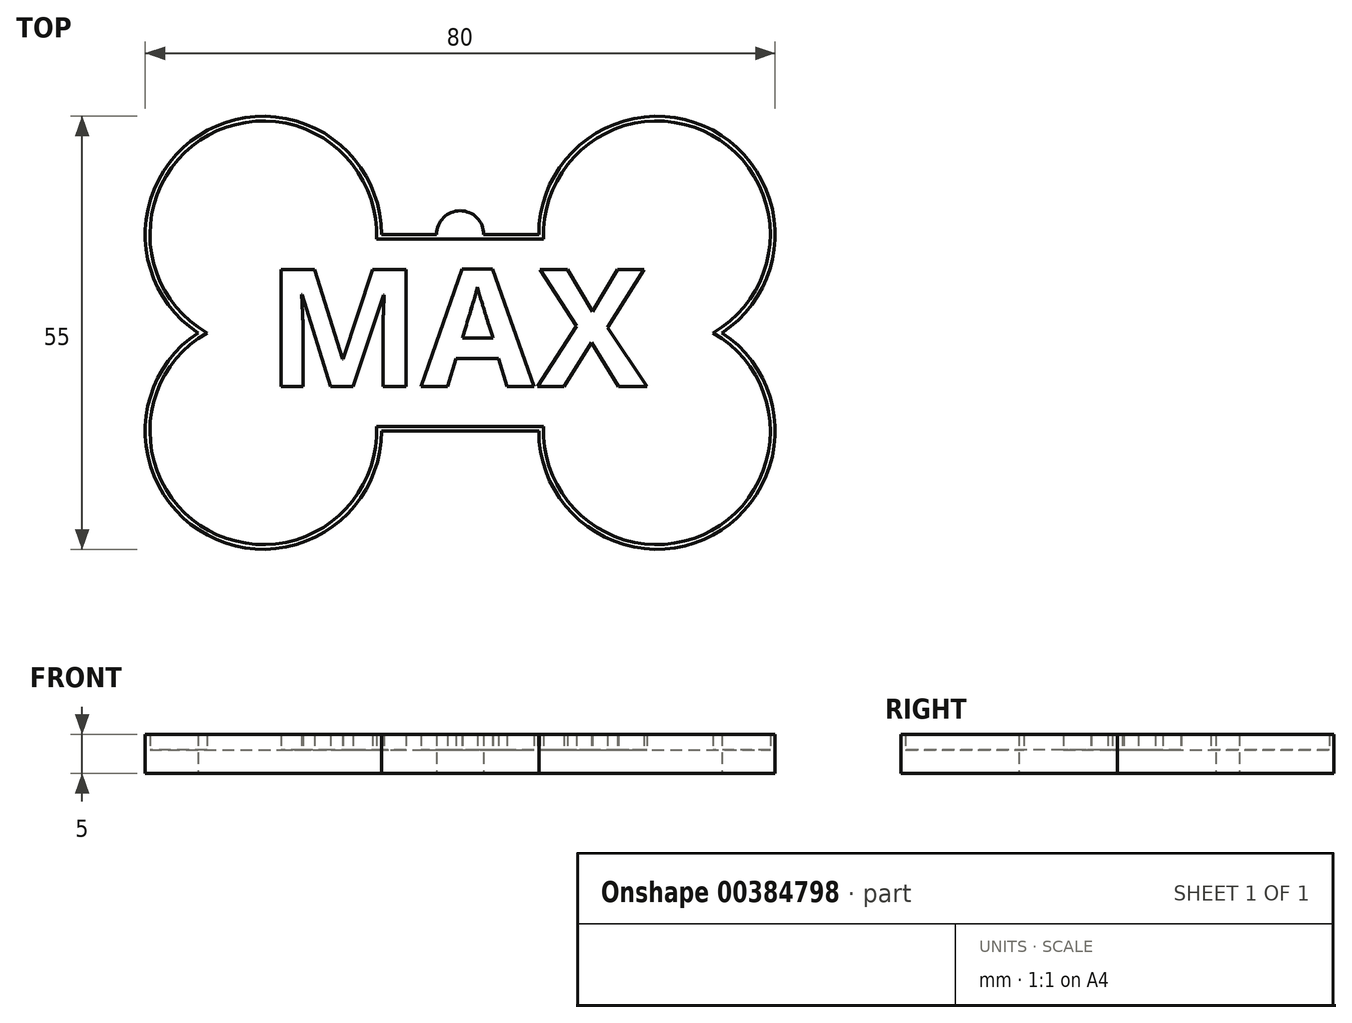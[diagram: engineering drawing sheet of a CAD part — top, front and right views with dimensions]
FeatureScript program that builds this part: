
annotation { "Feature Type Name" : "Feature", "Feature Type Description" : "" }
export const myFeature = defineFeature(function(context is Context, id is Id, definition is map)
    precondition{}
    {
        {
            var Q0;
            Q0=qCreatedBy(makeId("Top.planeOp"),FACE);
            var sketch = newSketch(context, id + "F0", { "sketchPlane" : qUnion([Q0])});
            skLineSegment(sketch, "E0.bottom", {"start": v(-10, 12.5) * mm, "end": v(-3, 12.5) * mm});
            skLineSegment(sketch, "E0.top", {"start": v(-10, -12.5) * mm, "end": v(10, -12.5) * mm});
            skArc(sketch, "E1", {"start": v(-10, 12.5) * mm, "mid": v(-32.1, 25.72) * mm, "end": v(-33.3, 0) * mm});
            skArc(sketch, "E2", {"start": v(33.3, 0) * mm, "mid": v(32.1, 25.72) * mm, "end": v(10, 12.5) * mm});
            skArc(sketch, "E3", {"start": v(-33.3, 0) * mm, "mid": v(-32.1, -25.72) * mm, "end": v(-10, -12.5) * mm});
            skArc(sketch, "E4", {"start": v(10, -12.5) * mm, "mid": v(32.1, -25.72) * mm, "end": v(33.3, 0) * mm});
            skArc(sketch, "E5", {"start": v(3, 12.5) * mm, "mid": v(0, 15.5) * mm, "end": v(-3, 12.5) * mm});
            skLineSegment(sketch, "E6.trimOffspring", {"start": v(3, 12.5) * mm, "end": v(10, 12.5) * mm});
            skSolve(sketch);
        }
        {
            var Q0;
            Q0 = qSketchRegion(id + "F0", true);
            extrude(context, id + "F1", {"entities" : qUnion([Q0]), "depth" : 3 * mm});
        }
        {
            var Q0;
            Q0=makeQuery(id+"F1.opExtrude","CAP_FACE",FACE,{"disambiguationData":[OSD([sQuery(id+"F0.wireOp",EDGE,"E0.bottom"),sQuery(id+"F0.wireOp",EDGE,"E0.top"),sQuery(id+"F0.wireOp",EDGE,"E1"),sQuery(id+"F0.wireOp",EDGE,"E2"),sQuery(id+"F0.wireOp",EDGE,"E3"),sQuery(id+"F0.wireOp",EDGE,"E4"),sQuery(id+"F0.wireOp",EDGE,"E5"),sQuery(id+"F0.wireOp",EDGE,"E6.trimOffspring")])],"isStart":false});
            var sketch = newSketch(context, id + "F2", { "sketchPlane" : qUnion([Q0])});
            skArc(sketch, "E7.0", {"start": v(-32.15, 0) * mm, "mid": v(-31.96, -25.1) * mm, "end": v(-10.61, -11.9) * mm});
            skArc(sketch, "E7.1", {"start": v(-10.61, 11.9) * mm, "mid": v(-31.96, 25.1) * mm, "end": v(-32.15, 0) * mm});
            skArc(sketch, "E7.2", {"start": v(10.61, -11.9) * mm, "mid": v(31.96, -25.1) * mm, "end": v(32.15, 0) * mm});
            skArc(sketch, "E7.3", {"start": v(32.15, 0) * mm, "mid": v(31.96, 25.1) * mm, "end": v(10.61, 11.9) * mm});
            skLineSegment(sketch, "E7.4", {"start": v(10.61, 11.9) * mm, "end": v(0, 11.9) * mm});
            skLineSegment(sketch, "E7.5", {"start": v(-10.61, -11.9) * mm, "end": v(10.61, -11.9) * mm});
            skLineSegment(sketch, "E7.6", {"start": v(0, 11.9) * mm, "end": v(-10.61, 11.9) * mm});
            skSolve(sketch);
        }
        {
            var Q0;
            Q0=makeQuery(id+"F2.imprint","IMPRINT",FACE,{"disambiguationData":[TD([[makeQuery(id+"F2.imprint","IMPRINT",EDGE,{"derivedFrom":sQuery(id+"F2.wireOp",EDGE,"E7.0")}),-1.0]])]});
            extrude(context, id + "F3", {"entities" : qUnion([Q0]), "operationType" : NewBodyOperationType.ADD, "depth" : 2 * mm});
        }
        {
            var Q0;
            Q0=makeQuery(id+"F1.opExtrude","CAP_FACE",FACE,{"disambiguationData":[OSD([sQuery(id+"F0.wireOp",EDGE,"E0.bottom"),sQuery(id+"F0.wireOp",EDGE,"E0.top"),sQuery(id+"F0.wireOp",EDGE,"E1"),sQuery(id+"F0.wireOp",EDGE,"E2"),sQuery(id+"F0.wireOp",EDGE,"E3"),sQuery(id+"F0.wireOp",EDGE,"E4"),sQuery(id+"F0.wireOp",EDGE,"E5"),sQuery(id+"F0.wireOp",EDGE,"E6.trimOffspring")])],"isStart":false});
            var sketch = newSketch(context, id + "F4", { "sketchPlane" : qUnion([Q0])});
            skText(sketch, "E8", { "text": "MAX", "fontName": "OpenSans-Bold.ttf"});
            const initialGuessF4  = {"E8": [-0.02463, -0.00684, 1, 0, 0.015]};
            skSetInitialGuess(sketch, initialGuessF4);
            skSolve(sketch);
        }
        {
            var Q0;
            Q0=makeQuery(id+"F4.imprint","IMPRINT",FACE,{"disambiguationData":[TD([[makeQuery(id+"F4.imprint","IMPRINT",EDGE,{"derivedFrom":sQuery(id+"F4.wireOp",EDGE,"E8.sketch_text.stroke-0")}),-1.0]])]});
            extrude(context, id + "F5", {"entities" : qUnion([Q0]), "operationType" : NewBodyOperationType.ADD, "depth" : 2 * mm});
        }
        {
            var Q0;
            Q0=makeQuery(id+"F4.imprint","IMPRINT",FACE,{"disambiguationData":[TD([[makeQuery(id+"F4.imprint","IMPRINT",EDGE,{"derivedFrom":sQuery(id+"F4.wireOp",EDGE,"E8.sketch_text.stroke-19")}),-1.0]])]});
            extrude(context, id + "F6", {"entities" : qUnion([Q0]), "operationType" : NewBodyOperationType.ADD, "depth" : 2 * mm});
        }
        {
            var Q0;
            Q0=makeQuery(id+"F4.imprint","IMPRINT",FACE,{"disambiguationData":[TD([[makeQuery(id+"F4.imprint","IMPRINT",EDGE,{"derivedFrom":sQuery(id+"F4.wireOp",EDGE,"E8.sketch_text.stroke-31")}),-1.0]])]});
            extrude(context, id + "F7", {"entities" : qUnion([Q0]), "operationType" : NewBodyOperationType.ADD, "depth" : 2 * mm});
        }
        {
            var Q0;
            Q0=makeQuery(id+"F4.imprint","IMPRINT",FACE,{"disambiguationData":[TD([[makeQuery(id+"F4.imprint","IMPRINT",EDGE,{"derivedFrom":sQuery(id+"F4.wireOp",EDGE,"E8.sketch_text.stroke-31")}),-1.0]])]});
            extrude(context, id + "F8", {"entities" : qUnion([Q0]), "operationType" : NewBodyOperationType.ADD, "depth" : 2 * mm});
        }
    });
